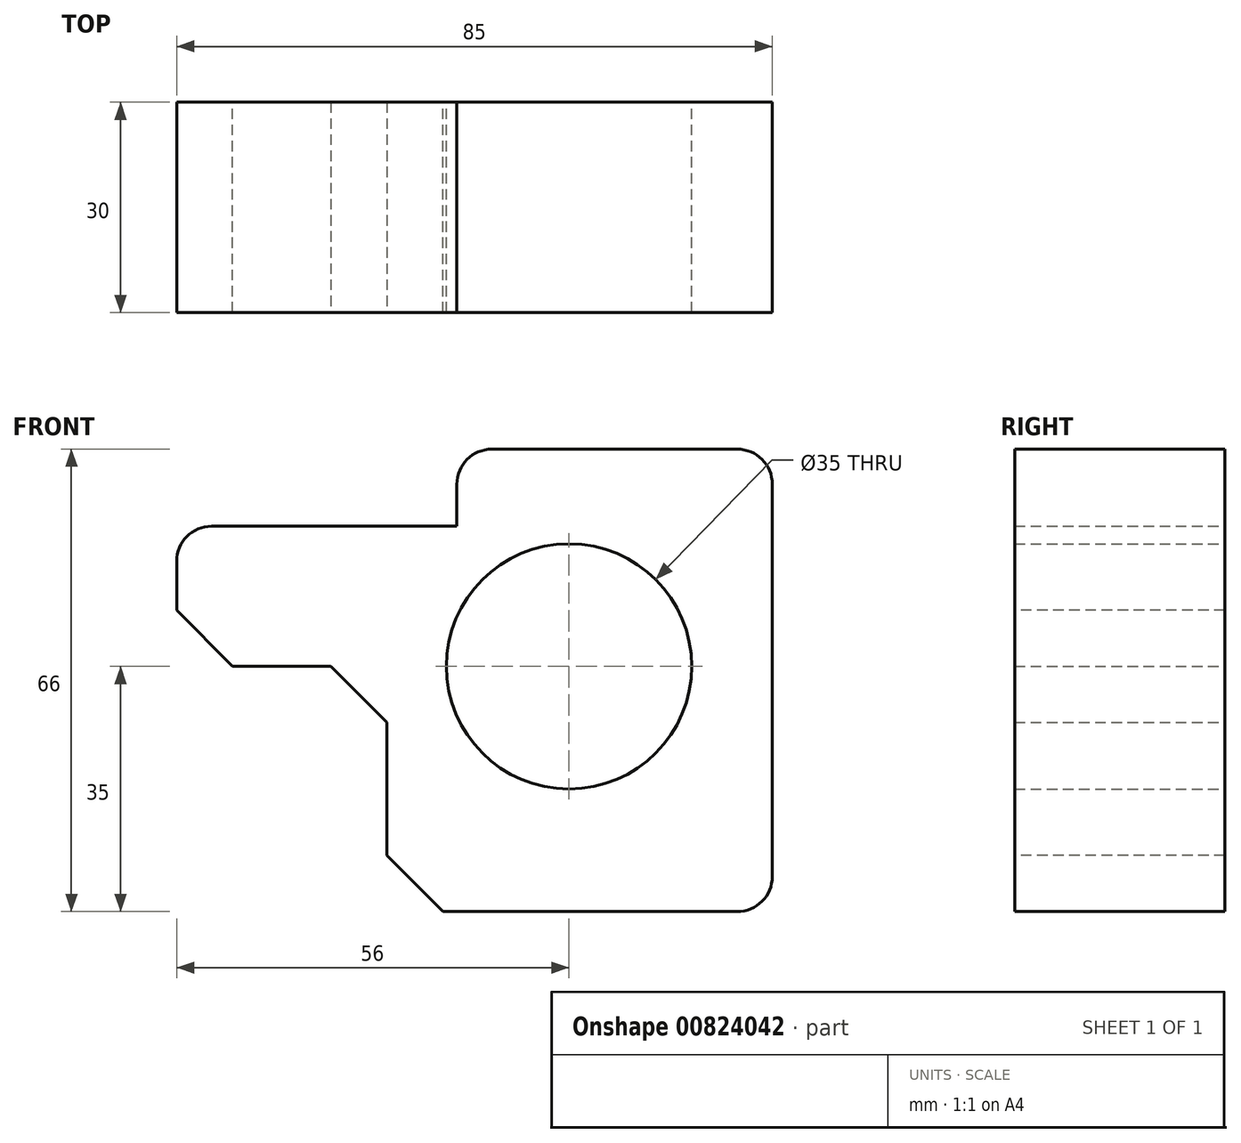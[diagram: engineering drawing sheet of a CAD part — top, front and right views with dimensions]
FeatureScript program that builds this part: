
annotation { "Feature Type Name" : "Feature", "Feature Type Description" : "" }
export const myFeature = defineFeature(function(context is Context, id is Id, definition is map)
    precondition{}
    {
        {
            var Q0;
            Q0=qCreatedBy(makeId("Front.planeOp"),FACE);
            var sketch = newSketch(context, id + "F0", { "sketchPlane" : qUnion([Q0])});
            skCircle(sketch, "E0", {"center": v(26, 35) * mm, "radius": 17.5 * mm});
            skLineSegment(sketch, "E1.bottom", {"start": v(0, 0) * mm, "end": v(55, 0) * mm});
            skLineSegment(sketch, "E1.top", {"start": v(10, 66) * mm, "end": v(55, 66) * mm});
            skLineSegment(sketch, "E1.left", {"start": v(0, 0) * mm, "end": v(0, 35) * mm});
            skLineSegment(sketch, "E1.right", {"start": v(55, 0) * mm, "end": v(55, 66) * mm});
            skLineSegment(sketch, "E2.bottom", {"start": v(10, 55) * mm, "end": v(-30, 55) * mm});
            skLineSegment(sketch, "E2.top", {"start": v(0, 35) * mm, "end": v(-30, 35) * mm});
            skLineSegment(sketch, "E2.right", {"start": v(-30, 55) * mm, "end": v(-30, 35) * mm});
            skLineSegment(sketch, "E3.trimOffspring", {"start": v(10, 55) * mm, "end": v(10, 66) * mm});
            skSolve(sketch);
        }
        {
            var Q0;
            Q0=makeQuery(id+"F0.imprint","IMPRINT",FACE,{"disambiguationData":[TD([[makeQuery(id+"F0.imprint","IMPRINT",EDGE,{"derivedFrom":sQuery(id+"F0.wireOp",EDGE,"E0")}),-1.0]])]});
            extrude(context, id + "F1", {"entities" : qUnion([Q0]), "depth" : 30 * mm, "offsetDistance" : 25 * mm});
        }
        {
            var Q0;
            Q0=makeQuery(id+"F1.opExtrude","SWEPT_EDGE",EDGE,{"disambiguationData":[OSD([sQuery(id+"F0.wireOp",EDGE,"E1.top"),sQuery(id+"F0.wireOp",EDGE,"E3.trimOffspring")])]});
            var Q1;
            Q1=makeQuery(id+"F1.opExtrude","SWEPT_EDGE",EDGE,{"disambiguationData":[OSD([sQuery(id+"F0.wireOp",EDGE,"E1.top"),sQuery(id+"F0.wireOp",EDGE,"E1.right")])]});
            var Q2;
            Q2=makeQuery(id+"F1.opExtrude","SWEPT_EDGE",EDGE,{"disambiguationData":[OSD([sQuery(id+"F0.wireOp",EDGE,"E1.bottom"),sQuery(id+"F0.wireOp",EDGE,"E1.right")])]});
            var Q3;
            Q3=makeQuery(id+"F1.opExtrude","SWEPT_EDGE",EDGE,{"disambiguationData":[OSD([sQuery(id+"F0.wireOp",EDGE,"E2.bottom"),sQuery(id+"F0.wireOp",EDGE,"E2.right")])]});
            fillet(context, id + "F2", {"entities" : qUnion([Q0, Q1, Q2, Q3]), "radius" : 5 * mm, "tangentPropagation" : true, "allowEdgeOverflow" : false});
        }
        {
            var Q0;
            Q0=makeQuery(id+"F1.opExtrude","SWEPT_EDGE",EDGE,{"disambiguationData":[OSD([sQuery(id+"F0.wireOp",EDGE,"E1.left"),sQuery(id+"F0.wireOp",EDGE,"E2.top")])]});
            var Q1;
            Q1=makeQuery(id+"F1.opExtrude","SWEPT_EDGE",EDGE,{"disambiguationData":[OSD([sQuery(id+"F0.wireOp",EDGE,"E2.top"),sQuery(id+"F0.wireOp",EDGE,"E2.right")])]});
            var Q2;
            Q2=makeQuery(id+"F1.opExtrude","SWEPT_EDGE",EDGE,{"disambiguationData":[OSD([sQuery(id+"F0.wireOp",EDGE,"E1.bottom"),sQuery(id+"F0.wireOp",EDGE,"E1.left")])]});
            chamfer(context, id + "F3", {"entities" : qUnion([Q0, Q1, Q2]), "width" : 8 * mm, "tangentPropagation" : true});
        }
    });
